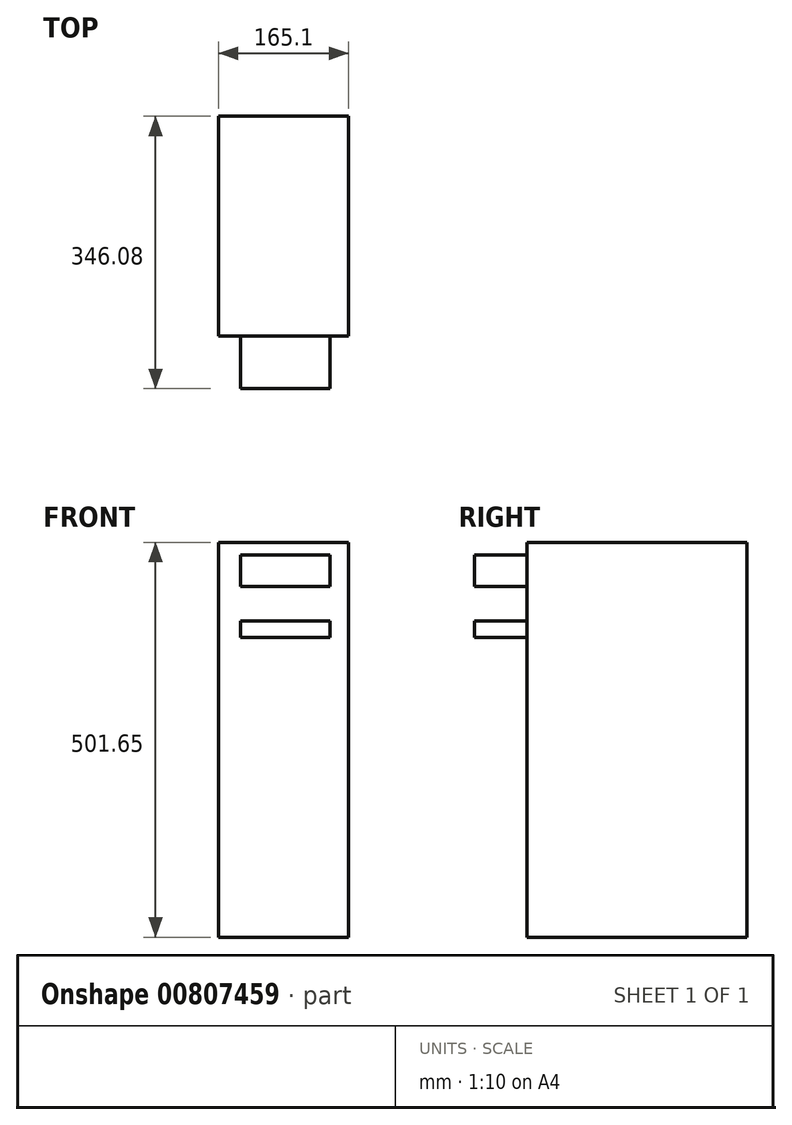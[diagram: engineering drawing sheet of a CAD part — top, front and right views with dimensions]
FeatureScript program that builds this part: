
annotation { "Feature Type Name" : "Feature", "Feature Type Description" : "" }
export const myFeature = defineFeature(function(context is Context, id is Id, definition is map)
    precondition{}
    {
        {
            var Q0;
            Q0=qCreatedBy(makeId("Front.planeOp"),FACE);
            var sketch = newSketch(context, id + "F0", { "sketchPlane" : qUnion([Q0])});
            skLineSegment(sketch, "E0.bottom", {"start": v(0, 0) * mm, "end": v(165.1, 0) * mm});
            skLineSegment(sketch, "E0.top", {"start": v(0, 501.65) * mm, "end": v(165.1, 501.65) * mm});
            skLineSegment(sketch, "E0.left", {"start": v(0, 0) * mm, "end": v(0, 501.65) * mm});
            skLineSegment(sketch, "E0.right", {"start": v(165.1, 0) * mm, "end": v(165.1, 501.65) * mm});
            skSolve(sketch);
        }
        {
            var Q0;
            Q0 = qSketchRegion(id + "F0", true);
            extrude(context, id + "F1", {"entities" : qUnion([Q0]), "depth" : 279.4 * mm, "offsetDistance" : 25.4 * mm});
        }
        {
            var Q0;
            Q0=makeQuery(id+"F1.opExtrude","CAP_FACE",FACE,{"disambiguationData":[OSD([sQuery(id+"F0.wireOp",EDGE,"E0.bottom"),sQuery(id+"F0.wireOp",EDGE,"E0.top"),sQuery(id+"F0.wireOp",EDGE,"E0.left"),sQuery(id+"F0.wireOp",EDGE,"E0.right")])],"isStart":false});
            var sketch = newSketch(context, id + "F2", { "sketchPlane" : qUnion([Q0])});
            skLineSegment(sketch, "E1.bottom", {"start": v(27.7, 485.65) * mm, "end": v(141.7, 485.65) * mm});
            skLineSegment(sketch, "E1.top", {"start": v(27.7, 445.65) * mm, "end": v(141.7, 445.65) * mm});
            skLineSegment(sketch, "E1.left", {"start": v(27.7, 485.65) * mm, "end": v(27.7, 445.65) * mm});
            skLineSegment(sketch, "E1.right", {"start": v(141.7, 485.65) * mm, "end": v(141.7, 445.65) * mm});
            skLineSegment(sketch, "E2.bottom", {"start": v(27.7, 401.65) * mm, "end": v(141.7, 401.65) * mm});
            skLineSegment(sketch, "E2.top", {"start": v(27.7, 380.65) * mm, "end": v(141.7, 380.65) * mm});
            skLineSegment(sketch, "E2.left", {"start": v(27.7, 401.65) * mm, "end": v(27.7, 380.65) * mm});
            skLineSegment(sketch, "E2.right", {"start": v(141.7, 401.65) * mm, "end": v(141.7, 380.65) * mm});
            skSolve(sketch);
        }
        {
            var Q0;
            Q0=makeQuery(id+"F2.imprint","IMPRINT",FACE,{"disambiguationData":[TD([[makeQuery(id+"F2.imprint","IMPRINT",EDGE,{"derivedFrom":sQuery(id+"F2.wireOp",EDGE,"E1.bottom")}),-1.0]])]});
            var Q1;
            Q1=makeQuery(id+"F2.imprint","IMPRINT",FACE,{"disambiguationData":[TD([[makeQuery(id+"F2.imprint","IMPRINT",EDGE,{"derivedFrom":sQuery(id+"F2.wireOp",EDGE,"E2.bottom")}),-1.0]])]});
            extrude(context, id + "F3", {"entities" : qUnion([Q0, Q1]), "operationType" : NewBodyOperationType.ADD, "depth" : 66.67 * mm, "offsetDistance" : 25.4 * mm});
        }
    });
